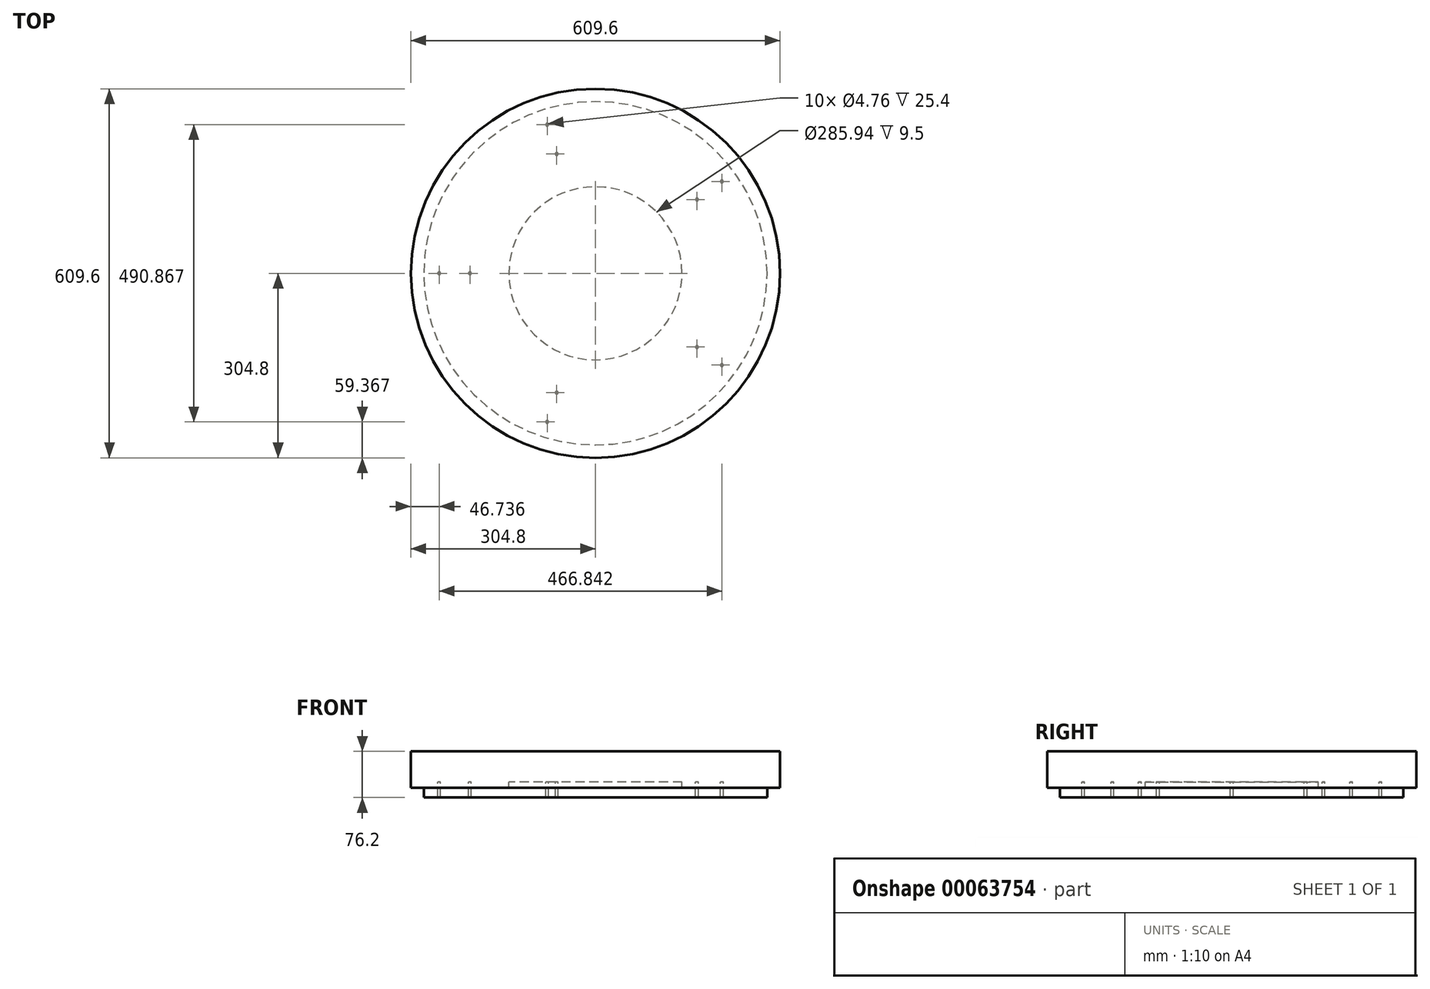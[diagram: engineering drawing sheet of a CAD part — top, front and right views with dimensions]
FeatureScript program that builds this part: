
annotation { "Feature Type Name" : "Feature", "Feature Type Description" : "" }
export const myFeature = defineFeature(function(context is Context, id is Id, definition is map)
    precondition{}
    {
        {
            assignVariable(context, id + "F0", {"name" : "H", "anyValue" : 15});
        }
        {
            assignVariable(context, id + "F1", {"name" : "S", "anyValue" : 5});
        }
        {
            var Q0;
            Q0=qCreatedBy(makeId("Top.planeOp"),FACE);
            var sketch = newSketch(context, id + "F2", { "sketchPlane" : qUnion([Q0])});
            skCircle(sketch, "E0", {"center": v(0, 0) * mm, "radius": 304.8 * mm});
            skCircle(sketch, "E1", {"center": v(0, 0) * mm, "radius": 292.1 * mm});
            skCircle(sketch, "E2.0", {"center": v(0, 0) * mm, "radius": 283.46 * mm});
            skSolve(sketch);
        }
        {
            var Q0;
            Q0=makeQuery(id+"F2.imprint","IMPRINT",FACE,{"disambiguationData":[TD([[makeQuery(id+"F2.imprint","IMPRINT",EDGE,{"derivedFrom":sQuery(id+"F2.wireOp",EDGE,"E1")}),1.0]])]});
            var Q1;
            Q1=sQuery(id+"F2.wireOp",EDGE,"E1");
            var Q2;
            Q2=sQuery(id+"F2.wireOp",EDGE,"E2.0");
            extrude(context, id + "F3", {"entities" : qUnion([Q0]), "surfaceEntities" : qUnion([Q1, Q2]), "depth" : (getVariable(context, 'H') - 5.5) * mm});
        }
        {
            var Q0;
            Q0=makeQuery(id+"F3.opExtrude","CAP_FACE",FACE,{"disambiguationData":[OSD([sQuery(id+"F2.wireOp",EDGE,"E1"),sQuery(id+"F2.wireOp",EDGE,"E2.0")])],"isStart":false});
            var sketch = newSketch(context, id + "F4", { "sketchPlane" : qUnion([Q0])});
            skCircle(sketch, "E3.0", {"center": v(0, 0) * mm, "radius": 283.46 * mm});
            skSolve(sketch);
        }
        {
            var Q0;
            Q0=qSketchRegion(id+"F4",true);
            extrude(context, id + "F5", {"entities" : qUnion([Q0]), "oppositeDirection" : true, "depth" : 25.4 * mm});
        }
        {
            var Q0;
            Q0=makeQuery(id+"F5.opExtrude","CAP_FACE",FACE,{"disambiguationData":[OSD([sQuery(id+"F4.wireOp",EDGE,"E3.0")])],"isStart":true});
            var sketch = newSketch(context, id + "F6", { "sketchPlane" : qUnion([Q0])});
            skLineSegment(sketch, "E4", {"start": v(-283.46, 0) * mm, "end": v(0, 0) * mm, "construction": true});
            skCircle(sketch, "E5.0", {"center": v(0, 0) * mm, "radius": 258.06 * mm, "construction": true});
            skCircle(sketch, "E6.0", {"center": v(0, 0) * mm, "radius": 207.26 * mm, "construction": true});
            skPoint(sketch, "E7", {"position": v(-258.06, 0) * mm});
            skPoint(sketch, "E8", {"position": v(-207.26, 0) * mm});
            skPoint(sketch, "E9.1.0", {"position": v(-64.05, -197.12) * mm});
            skPoint(sketch, "E9.1.1", {"position": v(-79.75, -245.43) * mm});
            skPoint(sketch, "E9.2.0", {"position": v(167.68, -121.83) * mm});
            skPoint(sketch, "E9.2.1", {"position": v(208.78, -151.69) * mm});
            skPoint(sketch, "E9.3.0", {"position": v(167.68, 121.83) * mm});
            skPoint(sketch, "E9.3.1", {"position": v(208.78, 151.69) * mm});
            skPoint(sketch, "E9.4.0", {"position": v(-64.05, 197.12) * mm});
            skPoint(sketch, "E9.4.1", {"position": v(-79.75, 245.43) * mm});
            skSolve(sketch);
        }
        {
            var Q0;
            Q0=sQuery(id+"F6.wireOp",VERTEX,"E7");
            var Q1;
            Q1=sQuery(id+"F6.wireOp",VERTEX,"E8");
            var Q2;
            Q2=sQuery(id+"F6.wireOp",VERTEX,"E9.4.1");
            var Q3;
            Q3=sQuery(id+"F6.wireOp",VERTEX,"E9.4.0");
            var Q4;
            Q4=sQuery(id+"F6.wireOp",VERTEX,"E9.3.0");
            var Q5;
            Q5=sQuery(id+"F6.wireOp",VERTEX,"E9.3.1");
            var Q6;
            Q6=sQuery(id+"F6.wireOp",VERTEX,"E9.2.0");
            var Q7;
            Q7=sQuery(id+"F6.wireOp",VERTEX,"E9.2.1");
            var Q8;
            Q8=sQuery(id+"F6.wireOp",VERTEX,"E9.1.1");
            var Q9;
            Q9=sQuery(id+"F6.wireOp",VERTEX,"E9.1.0");
            var Q10;
            Q10=sQuery(id+"F6.wireOp",VERTEX,"58d6160c-07d9-473b-a502-2546abea6cd9.1.6.0");
            var Q11;
            Q11=sQuery(id+"F6.wireOp",VERTEX,"58d6160c-07d9-473b-a502-2546abea6cd9.0.6.0");
            var Q12;
            Q12=sQuery(id+"F6.wireOp",VERTEX,"58d6160c-07d9-473b-a502-2546abea6cd9.0.5.0");
            var Q13;
            Q13=sQuery(id+"F6.wireOp",VERTEX,"58d6160c-07d9-473b-a502-2546abea6cd9.1.5.0");
            var Q14;
            Q14=makeQuery(id+"F5.opExtrude","SWEPT_BODY",BODY,{"disambiguationData":[OSD([sQuery(id+"F4.wireOp",EDGE,"E3.0")])]});
            hole(context, id + "F7", {"style" : HoleStyle.C_SINK, "holeDiameter" : 4.76 * mm, "cSinkDiameter" : 8.43 * mm, "endStyle" : HoleEndStyle.THROUGH, "locations" : qUnion([Q0, Q1, Q2, Q3, Q4, Q5, Q6, Q7, Q8, Q9, Q10, Q11, Q12, Q13]), "scope" : qUnion([Q14]), "cSinkAngle" : 90 * degree});
        }
        {
            var Q0;
            Q0=makeQuery(id+"F5.opExtrude","SWEPT_BODY",BODY,{"disambiguationData":[OSD([sQuery(id+"F4.wireOp",EDGE,"E3.0")])]});
            var Q1;
            Q1=qCreatedBy(makeId("Top.planeOp"),FACE);
            mirror(context, id + "F8", {"entities" : qUnion([Q0]), "mirrorPlane" : qUnion([Q1])});
        }
        {
            var Q0;
            Q0=makeQuery(id+"F8.opPattern","COPY",BODY,{"derivedFrom":makeQuery(id+"F5.opExtrude","SWEPT_BODY",BODY,{"disambiguationData":[OSD([sQuery(id+"F4.wireOp",EDGE,"E3.0")])]}),"instanceName":"1"});
            var Q1;
            Q1=makeQuery(id+"F5.opExtrude","CAP_FACE",FACE,{"disambiguationData":[OSD([sQuery(id+"F4.wireOp",EDGE,"E3.0")])],"isStart":true});
            transform(context, id + "F9", {"entities" : qUnion([Q0]), "transformType" : TransformType.TRANSLATION_3D, "dx" : 0 * mm, "dy" : 0 * mm, "dz" : (getVariable(context, 'H') - 5.5) * mm, "makeCopy" : false});
        }
        {
            var Q0;
            Q0=makeQuery(id+"F8.opPattern","COPY",FACE,{"derivedFrom":makeQuery(id+"F5.opExtrude","CAP_FACE",FACE,{"disambiguationData":[OSD([sQuery(id+"F4.wireOp",EDGE,"E3.0")])],"isStart":true}),"instanceName":"1"});
            var sketch = newSketch(context, id + "F10", { "sketchPlane" : qUnion([Q0])});
            skCircle(sketch, "E10.0", {"center": v(0, 0) * mm, "radius": 265.2 * mm, "construction": true});
            skCircle(sketch, "E11.0", {"center": v(0, 0) * mm, "radius": 228.7 * mm, "construction": true});
            skCircle(sketch, "E12.0", {"center": v(0, 0) * mm, "radius": 192.18 * mm, "construction": true});
            skLineSegment(sketch, "E13", {"start": v(0, 0) * mm, "end": v(0, 265.2) * mm, "construction": true});
            skLineSegment(sketch, "E14.0", {"start": v(22.23, 0) * mm, "end": v(22.23, 265.2) * mm, "construction": true});
            skLineSegment(sketch, "E15.0", {"start": v(-22.23, 0) * mm, "end": v(-22.23, 265.2) * mm, "construction": true});
            skPoint(sketch, "E16", {"position": v(-22.23, 227.61) * mm});
            skPoint(sketch, "E17", {"position": v(-22.23, 190.9) * mm});
            skPoint(sketch, "E18", {"position": v(22.23, 190.9) * mm});
            skPoint(sketch, "E19", {"position": v(22.23, 227.61) * mm});
            skPoint(sketch, "E20", {"position": v(22.23, 264.27) * mm});
            skPoint(sketch, "E21", {"position": v(-22.23, 264.27) * mm});
            skPoint(sketch, "E22.1.0", {"position": v(-188.42, 37.85) * mm});
            skPoint(sketch, "E22.1.1", {"position": v(-223.34, 49.2) * mm});
            skPoint(sketch, "E22.1.2", {"position": v(-258.2, 60.53) * mm});
            skPoint(sketch, "E22.1.3", {"position": v(-244.47, 102.8) * mm});
            skPoint(sketch, "E22.1.4", {"position": v(-209.6, 91.47) * mm});
            skPoint(sketch, "E22.1.5", {"position": v(-174.68, 80.13) * mm});
            skPoint(sketch, "E22.2.0", {"position": v(-94.22, -167.5) * mm});
            skPoint(sketch, "E22.2.1", {"position": v(-115.8, -197.2) * mm});
            skPoint(sketch, "E22.2.2", {"position": v(-137.36, -226.87) * mm});
            skPoint(sketch, "E22.2.3", {"position": v(-173.32, -200.74) * mm});
            skPoint(sketch, "E22.2.4", {"position": v(-151.77, -171.08) * mm});
            skPoint(sketch, "E22.2.5", {"position": v(-130.18, -141.37) * mm});
            skPoint(sketch, "E22.3.0", {"position": v(130.18, -141.37) * mm});
            skPoint(sketch, "E22.3.1", {"position": v(151.77, -171.08) * mm});
            skPoint(sketch, "E22.3.2", {"position": v(173.32, -200.74) * mm});
            skPoint(sketch, "E22.3.3", {"position": v(137.36, -226.87) * mm});
            skPoint(sketch, "E22.3.4", {"position": v(115.8, -197.2) * mm});
            skPoint(sketch, "E22.3.5", {"position": v(94.22, -167.5) * mm});
            skPoint(sketch, "E22.4.0", {"position": v(174.68, 80.13) * mm});
            skPoint(sketch, "E22.4.1", {"position": v(209.6, 91.47) * mm});
            skPoint(sketch, "E22.4.2", {"position": v(244.47, 102.8) * mm});
            skPoint(sketch, "E22.4.3", {"position": v(258.2, 60.53) * mm});
            skPoint(sketch, "E22.4.4", {"position": v(223.34, 49.2) * mm});
            skPoint(sketch, "E22.4.5", {"position": v(188.42, 37.85) * mm});
            skSolve(sketch);
        }
        {
            var Q0;
            Q0=sQuery(id+"F10.wireOp",VERTEX,"E21");
            var Q1;
            Q1=sQuery(id+"F10.wireOp",VERTEX,"E16");
            var Q2;
            Q2=sQuery(id+"F10.wireOp",VERTEX,"E17");
            var Q3;
            Q3=sQuery(id+"F10.wireOp",VERTEX,"E18");
            var Q4;
            Q4=sQuery(id+"F10.wireOp",VERTEX,"E19");
            var Q5;
            Q5=sQuery(id+"F10.wireOp",VERTEX,"E20");
            var Q6;
            Q6=sQuery(id+"F10.wireOp",VERTEX,"E22.4.0");
            var Q7;
            Q7=sQuery(id+"F10.wireOp",VERTEX,"E22.4.1");
            var Q8;
            Q8=sQuery(id+"F10.wireOp",VERTEX,"E22.4.2");
            var Q9;
            Q9=sQuery(id+"F10.wireOp",VERTEX,"E22.4.3");
            var Q10;
            Q10=sQuery(id+"F10.wireOp",VERTEX,"E22.4.4");
            var Q11;
            Q11=sQuery(id+"F10.wireOp",VERTEX,"E22.4.5");
            var Q12;
            Q12=sQuery(id+"F10.wireOp",VERTEX,"E22.3.0");
            var Q13;
            Q13=sQuery(id+"F10.wireOp",VERTEX,"E22.3.1");
            var Q14;
            Q14=sQuery(id+"F10.wireOp",VERTEX,"E22.3.2");
            var Q15;
            Q15=sQuery(id+"F10.wireOp",VERTEX,"E22.3.3");
            var Q16;
            Q16=sQuery(id+"F10.wireOp",VERTEX,"E22.3.4");
            var Q17;
            Q17=sQuery(id+"F10.wireOp",VERTEX,"E22.3.5");
            var Q18;
            Q18=sQuery(id+"F10.wireOp",VERTEX,"E22.2.2");
            var Q19;
            Q19=sQuery(id+"F10.wireOp",VERTEX,"E22.2.1");
            var Q20;
            Q20=sQuery(id+"F10.wireOp",VERTEX,"E22.2.0");
            var Q21;
            Q21=sQuery(id+"F10.wireOp",VERTEX,"E22.2.5");
            var Q22;
            Q22=sQuery(id+"F10.wireOp",VERTEX,"E22.2.4");
            var Q23;
            Q23=sQuery(id+"F10.wireOp",VERTEX,"E22.2.3");
            var Q24;
            Q24=sQuery(id+"F10.wireOp",VERTEX,"E22.1.0");
            var Q25;
            Q25=sQuery(id+"F10.wireOp",VERTEX,"E22.1.5");
            var Q26;
            Q26=sQuery(id+"F10.wireOp",VERTEX,"E22.1.1");
            var Q27;
            Q27=sQuery(id+"F10.wireOp",VERTEX,"E22.1.2");
            var Q28;
            Q28=sQuery(id+"F10.wireOp",VERTEX,"E22.1.3");
            var Q29;
            Q29=sQuery(id+"F10.wireOp",VERTEX,"E22.1.4");
            var Q30;
            Q30=makeQuery(id+"F8.opPattern","COPY",BODY,{"derivedFrom":makeQuery(id+"F5.opExtrude","SWEPT_BODY",BODY,{"disambiguationData":[OSD([sQuery(id+"F4.wireOp",EDGE,"E3.0")])]}),"instanceName":"1"});
            hole(context, id + "F11", {"style" : HoleStyle.SIMPLE, "holeDiameter" : 3.17 * mm, "endStyle" : HoleEndStyle.BLIND, "holeDepth" : 3.17 * mm, "locations" : qUnion([Q0, Q1, Q2, Q3, Q4, Q5, Q6, Q7, Q8, Q9, Q10, Q11, Q12, Q13, Q14, Q15, Q16, Q17, Q18, Q19, Q20, Q21, Q22, Q23, Q24, Q25, Q26, Q27, Q28, Q29]), "scope" : qUnion([Q30])});
        }
        {
            var Q0;
            Q0=makeQuery(id+"F8.opPattern","COPY",FACE,{"derivedFrom":makeQuery(id+"F5.opExtrude","CAP_FACE",FACE,{"disambiguationData":[OSD([sQuery(id+"F4.wireOp",EDGE,"E3.0")])],"isStart":false}),"instanceName":"1"});
            var sketch = newSketch(context, id + "F12", { "sketchPlane" : qUnion([Q0])});
            skCircle(sketch, "E23", {"center": v(0, 0) * mm, "radius": 142.97 * mm});
            skSolve(sketch);
        }
        {
            var Q0;
            Q0=qSketchRegion(id+"F12",true);
            extrude(context, id + "F13", {"entities" : qUnion([Q0]), "operationType" : NewBodyOperationType.REMOVE, "oppositeDirection" : true, "depth" : 25.4 * mm});
        }
        {
            var Q0;
            Q0=makeQuery(id+"F8.opPattern","COPY",FACE,{"derivedFrom":makeQuery(id+"F5.opExtrude","CAP_FACE",FACE,{"disambiguationData":[OSD([sQuery(id+"F4.wireOp",EDGE,"E3.0")])],"isStart":false}),"instanceName":"1"});
            var sketch = newSketch(context, id + "F14", { "sketchPlane" : qUnion([Q0])});
            skLineSegment(sketch, "E24", {"start": v(-258.06, 0) * mm, "end": v(-207.26, 0) * mm, "construction": true});
            skLineSegment(sketch, "E25.0", {"start": v(-283.46, 12.7) * mm, "end": v(-181.86, 12.7) * mm});
            skLineSegment(sketch, "E26.0", {"start": v(-283.46, -12.7) * mm, "end": v(-181.86, -12.7) * mm});
            skLineSegment(sketch, "E27", {"start": v(-283.46, -12.7) * mm, "end": v(-283.46, 12.7) * mm});
            skLineSegment(sketch, "E28", {"start": v(-181.86, -12.7) * mm, "end": v(-181.86, 12.7) * mm});
            skSolve(sketch);
        }
        {
            var Q0;
            Q0=qSketchRegion(id+"F14",true);
            extrude(context, id + "F15", {"entities" : qUnion([Q0]), "depth" : (getVariable(context, 'H') - 7.5) * mm});
        }
        {
            var Q0;
            Q0=makeQuery(id+"F15.opExtrude","SWEPT_BODY",BODY,{"disambiguationData":[OSD([sQuery(id+"F14.wireOp",EDGE,"E25.0"),sQuery(id+"F14.wireOp",EDGE,"E26.0"),sQuery(id+"F14.wireOp",EDGE,"E27"),sQuery(id+"F14.wireOp",EDGE,"E28")])]});
            var Q1;
            Q1=makeQuery(id+"F8.opPattern","COPY",EDGE,{"derivedFrom":makeQuery(id+"F5.opExtrude","CAP_EDGE",EDGE,{"disambiguationData":[OSD([sQuery(id+"F4.wireOp",EDGE,"E3.0")])],"isStart":false}),"instanceName":"1"});
            circularPattern(context, id + "F16", {"entities" : qUnion([Q0]), "axis" : qUnion([Q1]), "angle" : 360 * degree, "instanceCount" : round(getVariable(context, 'S')), "equalSpace" : true});
        }
        {
            var Q0;
            Q0=makeQuery(id+"F2.imprint","IMPRINT",FACE,{"disambiguationData":[TD([[makeQuery(id+"F2.imprint","IMPRINT",EDGE,{"derivedFrom":sQuery(id+"F2.wireOp",EDGE,"E0")}),1.0]])]});
            extrude(context, id + "F17", {"entities" : qUnion([Q0]), "depth" : (getVariable(context, 'H') - 5.5) * mm});
        }
        {
            var Q0;
            Q0=makeQuery(id+"F17.opExtrude","CAP_FACE",FACE,{"disambiguationData":[OSD([sQuery(id+"F2.wireOp",EDGE,"E0"),sQuery(id+"F2.wireOp",EDGE,"E1")])],"isStart":false});
            var sketch = newSketch(context, id + "F18", { "sketchPlane" : qUnion([Q0])});
            skCircle(sketch, "E29.0", {"center": v(0, 0) * mm, "radius": 304.8 * mm});
            skSolve(sketch);
        }
        {
            var Q0;
            Q0=qSketchRegion(id+"F18",true);
            extrude(context, id + "F19", {"entities" : qUnion([Q0]), "operationType" : NewBodyOperationType.ADD, "depth" : 50.8 * mm});
        }
    });
